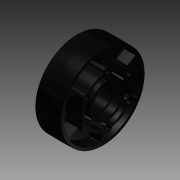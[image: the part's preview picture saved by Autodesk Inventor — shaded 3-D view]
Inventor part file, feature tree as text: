
AUTODESK INVENTOR PART (.ipt)
format: ipt  version: 2014 SP1 (Build 180222100, 222)  size: 1,163,264 bytes
history: native  units: in
note: dims shown in document units (in); Inventor stores cm internally (conversion verified against a paired STEP export)
features: fillet x2, imported_body x2, other x1
ambient origin geometry x8: Origin, YZ Plane, XZ Plane, XY Plane, X Axis, Y Axis, Z Axis, Center Point
bodies: Body1 (feature_tree), Body2 (feature_tree)
feature tree (5):
  fillet  "Fillet10"  [1 undecoded]
  other  "4in 2013 Hub1"
  fillet  "Fillet9"  [1 undecoded]
  imported_body  "Base1"
  imported_body  "Base2"
note: 2 required parameter values undecoded (feature->parameter linkage not recoverable at this tier; creation-order binding heuristic only, values carry confidence <= 0.55)
